# Revit family: Mechanical_Air-Curtain_Ready-Access_Heated-Fly-Fan
name_source: partatom
category: Mechanical Equipment
units: mm (PartAtom-declared; Revit-internal decimal feet)

## family parameters
Classification Number = 23.75.70.21.17
Cut with Voids When Loaded = No
Host = Face
Maintain Annotation Orientation = No
Part Type = Normal
Room Calculation Point = No
Round Connector Dimension = Use Diameter
Shared = No

## types (1)
- Mechanical_Air-Curtain_Ready-Access_Heated-Fly-Fan
    Assembly Code = D3090400
    Construction Details = http://www.arcat.com
    Default Elevation = 0' - 0"
    Description = Ready Access Product as Specified
    Electrical_Amperage = 0 A
    Electrical_Frequency = 0 Hz
    Electrical_Phase = 0
    Electrical_Voltage = 0 V
    Electrical_Wattage = 0 W
    Expected Lifespan (Years) = 0
    Frame Depth = 0' - 4"
    HVAC_Outlet Velocity = 0 FPM
    Keynote = 08582
    Maintenance Schedule (Months) = 0
    Manufacturer = Ready Access
    Manufacturer Fax = 630-876-7767
    Manufacturer Website = http://www.ready-access.com
    Model = As Specified
    Opening Width = 4' - 5 1/2"
    Product Data = http://www.arcat.com
    Revision = R1_2014-09
    Sales Information = http://www.ready-access.com
    Send Message = http://www.arcat.com
    Specification = http://www.arcat.com
    URL = http://www.ready-access.com
    Unit Height = 1' - 4"
    Unit Width = 4' - 5 1/2"
    Warranty Duration (Years) = 0

## geometry (parser evidence)
native form markers: Sweep x2
no freeform markers — native parametric forms only
